# Revit family: Haworth_Masters_Table-Rectangular
name_source: partatom
category: Furniture Systems
revit_build: Autodesk Revit 2018 (Build: 20170223_1515(x64)
units: mm (PartAtom-declared; Revit-internal decimal feet)

## family parameters
Always vertical = Yes
Cut with Voids When Loaded = No
OmniClass Number = 23.40.70.14.64.21
OmniClass Title = Systems Furniture
Part Type = Normal
Room Calculation Point = No
Round Connector Dimension = Use Diameter
Shared = No
Work Plane-Based = No

## types (22) — shared parameters
Actual Height = 30"
Assembly Code = E2020200
Custom Depth = No
Height = 30"
Leg Finish = Haworth _ Paint _ Metallic Champagne
Manufacturer = Haworth
Max. Width = 84"
Min. Height = 28 11/16"
Model = Masters
Revision Number = 0
Size = Verify Final Dim. w/ Haworth
Support Height = 28 13/16"
Support Offset = 1 1/4"
Sustainability Info = http://media.haworth.com
URL = http://www.haworth.com
URL - Product = http://www.haworth.com
Warranty = http://www.haworth.com
Worksurface Thickness = 1 3/16"

## per-type parameters (varying)
| type | Actual Depth | Actual Support Depth | Actual Width | Custom Size | Custom Width | Depth | Description | Height Adjustable | Hoop Leg | Max. Depth | Max. Height | Min. Depth | Min. Width | Min/Max Depth | Min/Max Height | Min/Max Width | Width |
| 29d 58w - Rectangular Top - Height Adjustable | 29" | 26 1/2" | 58" | No | No | 29" | 29d 58w - Rectangular Top - Height Adjustable | Yes | No | 41" | 47 3/16" | 29" | 52" | 29, 35, 41 in. | 28 11/16-47 11/16 in. | 58-82 in. @ 6 in. Incriments | 58" |
| 29d 64w - Rectangular Top - Height Adjustable | 29" | 26 1/2" | 64" | No | No | 29" | 29d 64w - Rectangular Top - Height Adjustable | Yes | No | 41" | 47 3/16" | 29" | 52" | 29, 35, 41 in. | 28 11/16-47 11/16 in. | 58-82 in. @ 6 in. Incriments | 64" |
| 29d 70w - Rectangular Top - Height Adjustable | 29" | 26 1/2" | 70" | Yes | Yes | 29" | 29d 70w - Rectangular Top - Height Adjustable | Yes | No | 41" | 47 3/16" | 29" | 52" | 29, 35, 41 in. | 28 11/16-47 11/16 in. | 58-82 in. @ 6 in. Incriments | 70" |
| 35d 58w - Rectangular Top - Height Adjustable | 35" | 32 1/2" | 58" | No | No | 35" | 35d 70w - Rectangular Top - Height Adjustable | Yes | No | 41" | 47 3/16" | 29" | 52" | 29, 35, 41 in. | 28 11/16-47 11/16 in. | 58-82 in. @ 6 in. Incriments | 58" |
| 35d 64w - Rectangular Top - Height Adjustable | 35" | 32 1/2" | 64" | No | No | 35" | 35d 70w - Rectangular Top - Height Adjustable | Yes | No | 41" | 47 3/16" | 29" | 52" | 29, 35, 41 in. | 28 11/16-47 11/16 in. | 58-82 in. @ 6 in. Incriments | 64" |
| 35d 70w - Rectangular Top - Height Adjustable | 35" | 32 1/2" | 70" | Yes | Yes | 35" | 35d 70w - Rectangular Top - Height Adjustable | Yes | No | 41" | 47 3/16" | 29" | 52" | 29, 35, 41 in. | 28 11/16-47 11/16 in. | 58-82 in. @ 6 in. Incriments | 70" |
| 35d 76w - Rectangular Top - Height Adjustable | 35" | 32 1/2" | 76" | Yes | Yes | 35" | 35d 76w - Rectangular Top - Height Adjustable | Yes | No | 41" | 47 3/16" | 29" | 52" | 29, 35, 41 in. | 28 11/16-47 11/16 in. | 58-82 in. @ 6 in. Incriments | 76" |
| 35d 82w - Rectangular Top - Height Adjustable | 35" | 32 1/2" | 82" | No | No | 35" | 35d 82w - Rectangular Top - Height Adjustable | Yes | No | 41" | 47 3/16" | 29" | 52" | 29, 35, 41 in. | 28 11/16-47 11/16 in. | 58-82 in. @ 6 in. Incriments | 82" |
| 41d 70w - Rectangular Top - Height Adjustable | 41" | 38 1/2" | 70" | Yes | Yes | 41" | 42d 70w - Rectangular Top - Height Adjustable | Yes | No | 41" | 47 3/16" | 29" | 52" | 29, 35, 41 in. | 28 11/16-47 11/16 in. | 58-82 in. @ 6 in. Incriments | 70" |
| 41d 76w - Rectangular Top - Height Adjustable | 41" | 38 1/2" | 76" | Yes | Yes | 41" | 42d 76w - Rectangular Top - Height Adjustable | Yes | No | 41" | 47 3/16" | 29" | 52" | 29, 35, 41 in. | 28 11/16-47 11/16 in. | 58-82 in. @ 6 in. Incriments | 76" |
| 41d 82w - Rectangular Top - Height Adjustable | 41" | 38 1/2" | 82" | No | No | 41" | 42d 82w - Rectangular Top - Height Adjustable | Yes | No | 41" | 47 3/16" | 29" | 52" | 29, 35, 41 in. | 28 11/16-47 11/16 in. | 58-82 in. @ 6 in. Incriments | 82" |
| 30d 60w - Rectangular Top - Hoop | 30" | 27 1/2" | 60" | No | No | 30" | 30d 60w - Rectangular Top - Hoop | No | Yes | 42" | 32 11/16" | 30" | 60" | 30, 36, 42 in. | 28 11/16-32 11/16 in. | 60-84 in. @ 6 in. Increments | 60" |
| 30d 66w - Rectangular Top - Hoop | 30" | 27 1/2" | 66" | No | No | 30" | 30d 66w - Rectangular Top - Hoop | No | Yes | 42" | 32 11/16" | 30" | 60" | 30, 36, 42 in. | 28 11/16-32 11/16 in. | 60-84 in. @ 6 in. Increments | 66" |
| 30d 72w - Rectangular Top - Hoop | 30" | 27 1/2" | 72" | Yes | Yes | 30" | 30d 72w - Rectangular Top - Hoop | No | Yes | 42" | 32 11/16" | 30" | 60" | 30, 36, 42 in. | 28 11/16-32 11/16 in. | 60-84 in. @ 6 in. Increments | 72" |
| 36d 60w - Rectangular Top - Hoop | 36" | 33 1/2" | 60" | No | No | 36" | 36d 60w - Rectangular Top - Hoop | No | Yes | 42" | 32 11/16" | 30" | 60" | 30, 36, 42 in. | 28 11/16-32 11/16 in. | 60-84 in. @ 6 in. Increments | 60" |
| 36d 66w - Rectangular Top - Hoop | 36" | 33 1/2" | 66" | No | No | 36" | 36d 66w - Rectangular Top - Hoop | No | Yes | 42" | 32 11/16" | 30" | 60" | 30, 36, 42 in. | 28 11/16-32 11/16 in. | 60-84 in. @ 6 in. Increments | 66" |
| 36d 72w - Rectangular Top - Hoop | 36" | 33 1/2" | 72" | Yes | Yes | 36" | 36d 72w - Rectangular Top - Hoop | No | Yes | 42" | 32 11/16" | 30" | 60" | 30, 36, 42 in. | 28 11/16-32 11/16 in. | 60-84 in. @ 6 in. Increments | 72" |
| 36d 78w - Rectangular Top - Hoop | 36" | 33 1/2" | 78" | Yes | Yes | 36" | 36d 78w - Rectangular Top - Hoop | No | Yes | 42" | 32 11/16" | 30" | 60" | 30, 36, 42 in. | 28 11/16-32 11/16 in. | 60-84 in. @ 6 in. Increments | 78" |
| 36d 84w - Rectangular Top - Hoop | 36" | 33 1/2" | 84" | No | No | 36" | 36d 84w - Rectangular Top - Hoop | No | Yes | 42" | 32 11/16" | 30" | 60" | 30, 36, 42 in. | 28 11/16-32 11/16 in. | 60-84 in. @ 6 in. Increments | 84" |
| 42d 72w - Rectangular Top - Hoop | 42" | 39 1/2" | 72" | Yes | Yes | 42" | 42d 72w - Rectangular Top - Hoop | No | Yes | 42" | 32 11/16" | 30" | 60" | 30, 36, 42 in. | 28 11/16-32 11/16 in. | 60-84 in. @ 6 in. Increments | 72" |
| 42d 78w - Rectangular Top - Hoop | 42" | 39 1/2" | 78" | Yes | Yes | 42" | 42d 78w - Rectangular Top - Hoop | No | Yes | 42" | 32 11/16" | 30" | 60" | 30, 36, 42 in. | 28 11/16-32 11/16 in. | 60-84 in. @ 6 in. Increments | 78" |
| 42d 84w - Rectangular Top - Hoop | 42" | 39 1/2" | 84" | No | No | 42" | 42d 84w - Rectangular Top - Hoop | No | Yes | 42" | 32 11/16" | 30" | 60" | 30, 36, 42 in. | 28 11/16-32 11/16 in. | 60-84 in. @ 6 in. Increments | 84" |

## geometry (parser evidence)
native form markers: Sweep x9
no freeform markers — native parametric forms only
